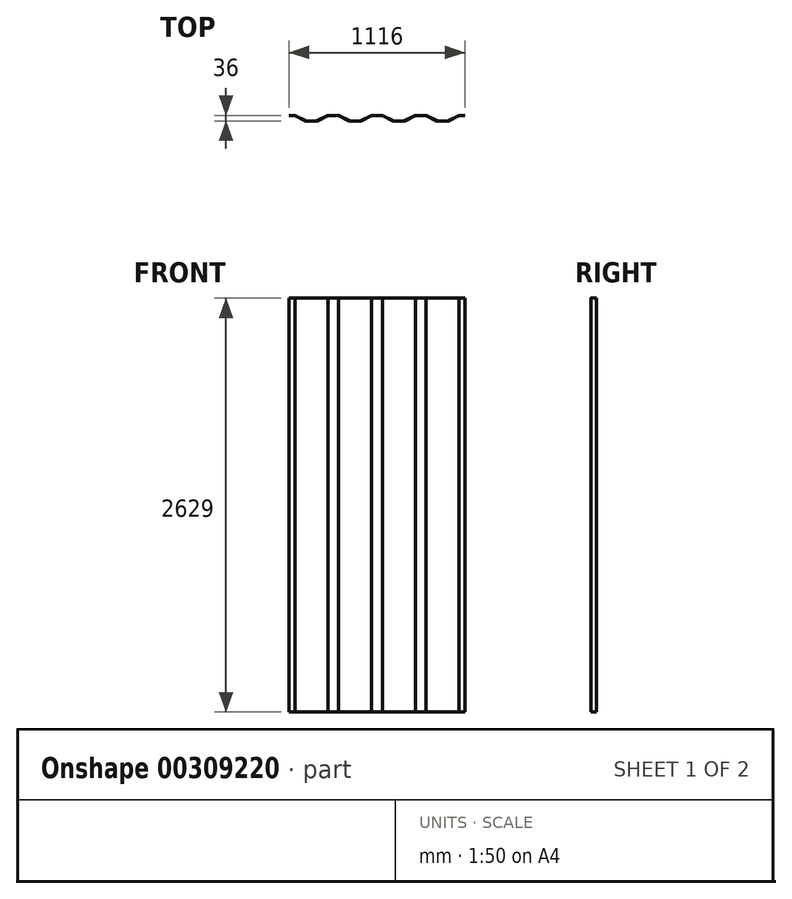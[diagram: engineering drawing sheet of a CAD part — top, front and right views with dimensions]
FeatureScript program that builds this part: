
annotation { "Feature Type Name" : "Feature", "Feature Type Description" : "" }
export const myFeature = defineFeature(function(context is Context, id is Id, definition is map)
    precondition{}
    {
        {
            var Q0;
            Q0=qCreatedBy(makeId("Top.planeOp"),FACE);
            var sketch = newSketch(context, id + "F0", { "sketchPlane" : qUnion([Q0])});
            skLineSegment(sketch, "E0", {"start": v(0, 0) * mm, "end": v(1116, 0) * mm});
            skLineSegment(sketch, "E1", {"start": v(0, 15.22) * mm, "end": v(37, 15.22) * mm});
            skLineSegment(sketch, "E2", {"start": v(37, 15.22) * mm, "end": v(105, 15.22) * mm});
            skLineSegment(sketch, "E3", {"start": v(105, 15.22) * mm, "end": v(177, 15.22) * mm});
            skLineSegment(sketch, "E4", {"start": v(177, 15.22) * mm, "end": v(245, 15.22) * mm});
            skLineSegment(sketch, "E5", {"start": v(245, 15.22) * mm, "end": v(315, 15.22) * mm});
            skLineSegment(sketch, "E6", {"start": v(315, 15.22) * mm, "end": v(383, 15.22) * mm});
            skLineSegment(sketch, "E7", {"start": v(383, 15.22) * mm, "end": v(455, 15.22) * mm});
            skLineSegment(sketch, "E8", {"start": v(455, 15.22) * mm, "end": v(523, 15.22) * mm});
            skLineSegment(sketch, "E9", {"start": v(523, 15.22) * mm, "end": v(593, 15.22) * mm});
            skLineSegment(sketch, "E10", {"start": v(593, 15.22) * mm, "end": v(661, 15.22) * mm});
            skLineSegment(sketch, "E11", {"start": v(661, 15.22) * mm, "end": v(733, 15.22) * mm});
            skLineSegment(sketch, "E12", {"start": v(733, 15.22) * mm, "end": v(801, 15.22) * mm});
            skLineSegment(sketch, "E13", {"start": v(801, 15.22) * mm, "end": v(871, 15.22) * mm});
            skLineSegment(sketch, "E14", {"start": v(871, 15.22) * mm, "end": v(939, 15.22) * mm});
            skLineSegment(sketch, "E15", {"start": v(939, 15.22) * mm, "end": v(1011, 15.22) * mm});
            skLineSegment(sketch, "E16", {"start": v(1011, 15.22) * mm, "end": v(1079, 15.22) * mm});
            skLineSegment(sketch, "E17", {"start": v(1079, 15.22) * mm, "end": v(1116, 15.22) * mm});
            skLineSegment(sketch, "E18", {"start": v(1116, 15.22) * mm, "end": v(1116, 51.22) * mm});
            skLineSegment(sketch, "E19", {"start": v(1124.7, 15.22) * mm, "end": v(1124.7, 16.82) * mm});
            skLineSegment(sketch, "E20", {"start": v(1116, 51.22) * mm, "end": v(1080.2, 51.22) * mm});
            skLineSegment(sketch, "E21", {"start": v(1077.94, 50.68) * mm, "end": v(1012.06, 17.36) * mm});
            skLineSegment(sketch, "E22", {"start": v(1009.8, 16.82) * mm, "end": v(940.2, 16.82) * mm});
            skLineSegment(sketch, "E23", {"start": v(937.94, 17.36) * mm, "end": v(872.06, 50.68) * mm});
            skLineSegment(sketch, "E24", {"start": v(869.8, 51.22) * mm, "end": v(802.2, 51.22) * mm});
            skLineSegment(sketch, "E25", {"start": v(799.94, 50.68) * mm, "end": v(734.06, 17.36) * mm});
            skLineSegment(sketch, "E26", {"start": v(731.8, 16.82) * mm, "end": v(662.2, 16.82) * mm});
            skLineSegment(sketch, "E27", {"start": v(659.94, 17.36) * mm, "end": v(594.06, 50.68) * mm});
            skLineSegment(sketch, "E28", {"start": v(591.8, 51.22) * mm, "end": v(524.2, 51.22) * mm});
            skLineSegment(sketch, "E29", {"start": v(456.06, 17.36) * mm, "end": v(521.94, 50.68) * mm});
            skLineSegment(sketch, "E30", {"start": v(453.8, 16.82) * mm, "end": v(384.2, 16.82) * mm});
            skLineSegment(sketch, "E31", {"start": v(381.94, 17.36) * mm, "end": v(316.06, 50.68) * mm});
            skLineSegment(sketch, "E32", {"start": v(313.8, 51.22) * mm, "end": v(246.2, 51.22) * mm});
            skLineSegment(sketch, "E33", {"start": v(243.94, 50.68) * mm, "end": v(178.06, 17.36) * mm});
            skLineSegment(sketch, "E34", {"start": v(175.8, 16.82) * mm, "end": v(106.2, 16.82) * mm});
            skLineSegment(sketch, "E35", {"start": v(103.94, 17.36) * mm, "end": v(38.06, 50.68) * mm});
            skLineSegment(sketch, "E36", {"start": v(35.8, 51.22) * mm, "end": v(0, 51.22) * mm});
            skPoint(sketch, "E37.visualSharp", {"position": v(1079, 51.22) * mm});
            skArc(sketch, "E37.filletArc", {"start": v(1080.2, 51.22) * mm, "mid": v(1079.03, 51.09) * mm, "end": v(1077.94, 50.68) * mm});
            skPoint(sketch, "E38.visualSharp", {"position": v(1011, 16.82) * mm});
            skArc(sketch, "E38.filletArc", {"start": v(1009.8, 16.82) * mm, "mid": v(1010.97, 16.96) * mm, "end": v(1012.06, 17.36) * mm});
            skPoint(sketch, "E39.visualSharp", {"position": v(939, 16.82) * mm});
            skArc(sketch, "E39.filletArc", {"start": v(937.94, 17.36) * mm, "mid": v(939.03, 16.96) * mm, "end": v(940.2, 16.82) * mm});
            skPoint(sketch, "E40.visualSharp", {"position": v(871, 51.22) * mm});
            skArc(sketch, "E40.filletArc", {"start": v(872.06, 50.68) * mm, "mid": v(870.97, 51.09) * mm, "end": v(869.8, 51.22) * mm});
            skPoint(sketch, "E41.visualSharp", {"position": v(801, 51.22) * mm});
            skArc(sketch, "E41.filletArc", {"start": v(802.2, 51.22) * mm, "mid": v(801.03, 51.09) * mm, "end": v(799.94, 50.68) * mm});
            skPoint(sketch, "E42.visualSharp", {"position": v(733, 16.82) * mm});
            skArc(sketch, "E42.filletArc", {"start": v(731.8, 16.82) * mm, "mid": v(732.97, 16.96) * mm, "end": v(734.06, 17.36) * mm});
            skPoint(sketch, "E43.visualSharp", {"position": v(661, 16.82) * mm});
            skArc(sketch, "E43.filletArc", {"start": v(659.94, 17.36) * mm, "mid": v(661.03, 16.96) * mm, "end": v(662.2, 16.82) * mm});
            skPoint(sketch, "E44.visualSharp", {"position": v(593, 51.22) * mm});
            skArc(sketch, "E44.filletArc", {"start": v(594.06, 50.68) * mm, "mid": v(592.97, 51.09) * mm, "end": v(591.8, 51.22) * mm});
            skPoint(sketch, "E45.visualSharp", {"position": v(523, 51.22) * mm});
            skArc(sketch, "E45.filletArc", {"start": v(524.2, 51.22) * mm, "mid": v(523.03, 51.09) * mm, "end": v(521.94, 50.68) * mm});
            skPoint(sketch, "E46.visualSharp", {"position": v(455, 16.82) * mm});
            skArc(sketch, "E46.filletArc", {"start": v(453.8, 16.82) * mm, "mid": v(454.97, 16.96) * mm, "end": v(456.06, 17.36) * mm});
            skPoint(sketch, "E47.visualSharp", {"position": v(383, 16.82) * mm});
            skArc(sketch, "E47.filletArc", {"start": v(381.94, 17.36) * mm, "mid": v(383.03, 16.96) * mm, "end": v(384.2, 16.82) * mm});
            skPoint(sketch, "E48.visualSharp", {"position": v(315, 51.22) * mm});
            skArc(sketch, "E48.filletArc", {"start": v(316.06, 50.68) * mm, "mid": v(314.97, 51.09) * mm, "end": v(313.8, 51.22) * mm});
            skPoint(sketch, "E49.visualSharp", {"position": v(245, 51.22) * mm});
            skArc(sketch, "E49.filletArc", {"start": v(246.2, 51.22) * mm, "mid": v(245.03, 51.09) * mm, "end": v(243.94, 50.68) * mm});
            skPoint(sketch, "E50.visualSharp", {"position": v(177, 16.82) * mm});
            skArc(sketch, "E50.filletArc", {"start": v(175.8, 16.82) * mm, "mid": v(176.97, 16.96) * mm, "end": v(178.06, 17.36) * mm});
            skPoint(sketch, "E51.visualSharp", {"position": v(37, 51.22) * mm});
            skArc(sketch, "E51.filletArc", {"start": v(38.06, 50.68) * mm, "mid": v(36.97, 51.09) * mm, "end": v(35.8, 51.22) * mm});
            skPoint(sketch, "E52.visualSharp", {"position": v(105, 16.82) * mm});
            skArc(sketch, "E52.filletArc", {"start": v(103.94, 17.36) * mm, "mid": v(105.03, 16.96) * mm, "end": v(106.2, 16.82) * mm});
            skLineSegment(sketch, "E53.0", {"start": v(36.62, 49.62) * mm, "end": v(0, 49.62) * mm});
            skLineSegment(sketch, "E53.1", {"start": v(103.21, 15.93) * mm, "end": v(36.62, 49.62) * mm});
            skArc(sketch, "E53.2", {"start": v(103.21, 15.93) * mm, "mid": v(104.66, 15.4) * mm, "end": v(106.2, 15.22) * mm});
            skLineSegment(sketch, "E53.3", {"start": v(731.8, 15.22) * mm, "end": v(662.2, 15.22) * mm});
            skArc(sketch, "E53.4", {"start": v(731.8, 15.22) * mm, "mid": v(733.34, 15.4) * mm, "end": v(734.79, 15.93) * mm});
            skLineSegment(sketch, "E53.5", {"start": v(801.38, 49.62) * mm, "end": v(734.79, 15.93) * mm});
            skLineSegment(sketch, "E53.6", {"start": v(870.62, 49.62) * mm, "end": v(801.38, 49.62) * mm});
            skLineSegment(sketch, "E53.7", {"start": v(937.21, 15.93) * mm, "end": v(870.62, 49.62) * mm});
            skArc(sketch, "E53.8", {"start": v(937.21, 15.93) * mm, "mid": v(938.66, 15.4) * mm, "end": v(940.2, 15.22) * mm});
            skLineSegment(sketch, "E53.9", {"start": v(1116, 49.62) * mm, "end": v(1079.38, 49.62) * mm});
            skLineSegment(sketch, "E53.10", {"start": v(1079.38, 49.62) * mm, "end": v(1012.79, 15.93) * mm});
            skArc(sketch, "E53.11", {"start": v(1009.8, 15.22) * mm, "mid": v(1011.34, 15.4) * mm, "end": v(1012.79, 15.93) * mm});
            skLineSegment(sketch, "E53.12", {"start": v(1009.8, 15.22) * mm, "end": v(940.2, 15.22) * mm});
            skArc(sketch, "E53.13", {"start": v(659.21, 15.93) * mm, "mid": v(660.66, 15.4) * mm, "end": v(662.2, 15.22) * mm});
            skLineSegment(sketch, "E53.14", {"start": v(659.21, 15.93) * mm, "end": v(592.62, 49.62) * mm});
            skLineSegment(sketch, "E53.15", {"start": v(592.62, 49.62) * mm, "end": v(523.38, 49.62) * mm});
            skLineSegment(sketch, "E53.16", {"start": v(456.79, 15.93) * mm, "end": v(523.38, 49.62) * mm});
            skArc(sketch, "E53.17", {"start": v(453.8, 15.22) * mm, "mid": v(455.34, 15.4) * mm, "end": v(456.79, 15.93) * mm});
            skLineSegment(sketch, "E53.18", {"start": v(453.8, 15.22) * mm, "end": v(384.2, 15.22) * mm});
            skArc(sketch, "E53.19", {"start": v(381.21, 15.93) * mm, "mid": v(382.66, 15.4) * mm, "end": v(384.2, 15.22) * mm});
            skLineSegment(sketch, "E53.20", {"start": v(381.21, 15.93) * mm, "end": v(314.62, 49.62) * mm});
            skLineSegment(sketch, "E53.21", {"start": v(314.62, 49.62) * mm, "end": v(245.38, 49.62) * mm});
            skLineSegment(sketch, "E53.22", {"start": v(245.38, 49.62) * mm, "end": v(178.79, 15.93) * mm});
            skArc(sketch, "E53.23", {"start": v(175.8, 15.22) * mm, "mid": v(177.34, 15.4) * mm, "end": v(178.79, 15.93) * mm});
            skLineSegment(sketch, "E53.24", {"start": v(175.8, 15.22) * mm, "end": v(106.2, 15.22) * mm});
            skLineSegment(sketch, "E54", {"start": v(0, 51.22) * mm, "end": v(0, 49.62) * mm});
            skSolve(sketch);
        }
        {
            var Q0;
            {var subQ1=sQuery(id+"F0.wireOp",EDGE,"E20");Q0=makeQuery(id+"F0.imprint","IMPRINT",FACE,{"disambiguationData":[TD([[makeQuery(id+"F0.imprint","IMPRINT",EDGE,{"derivedFrom":subQ1}),1.0]])]});}
            extrude(context, id + "F1", {"entities" : qUnion([Q0]), "depth" : 2629 * mm});
        }
    });
